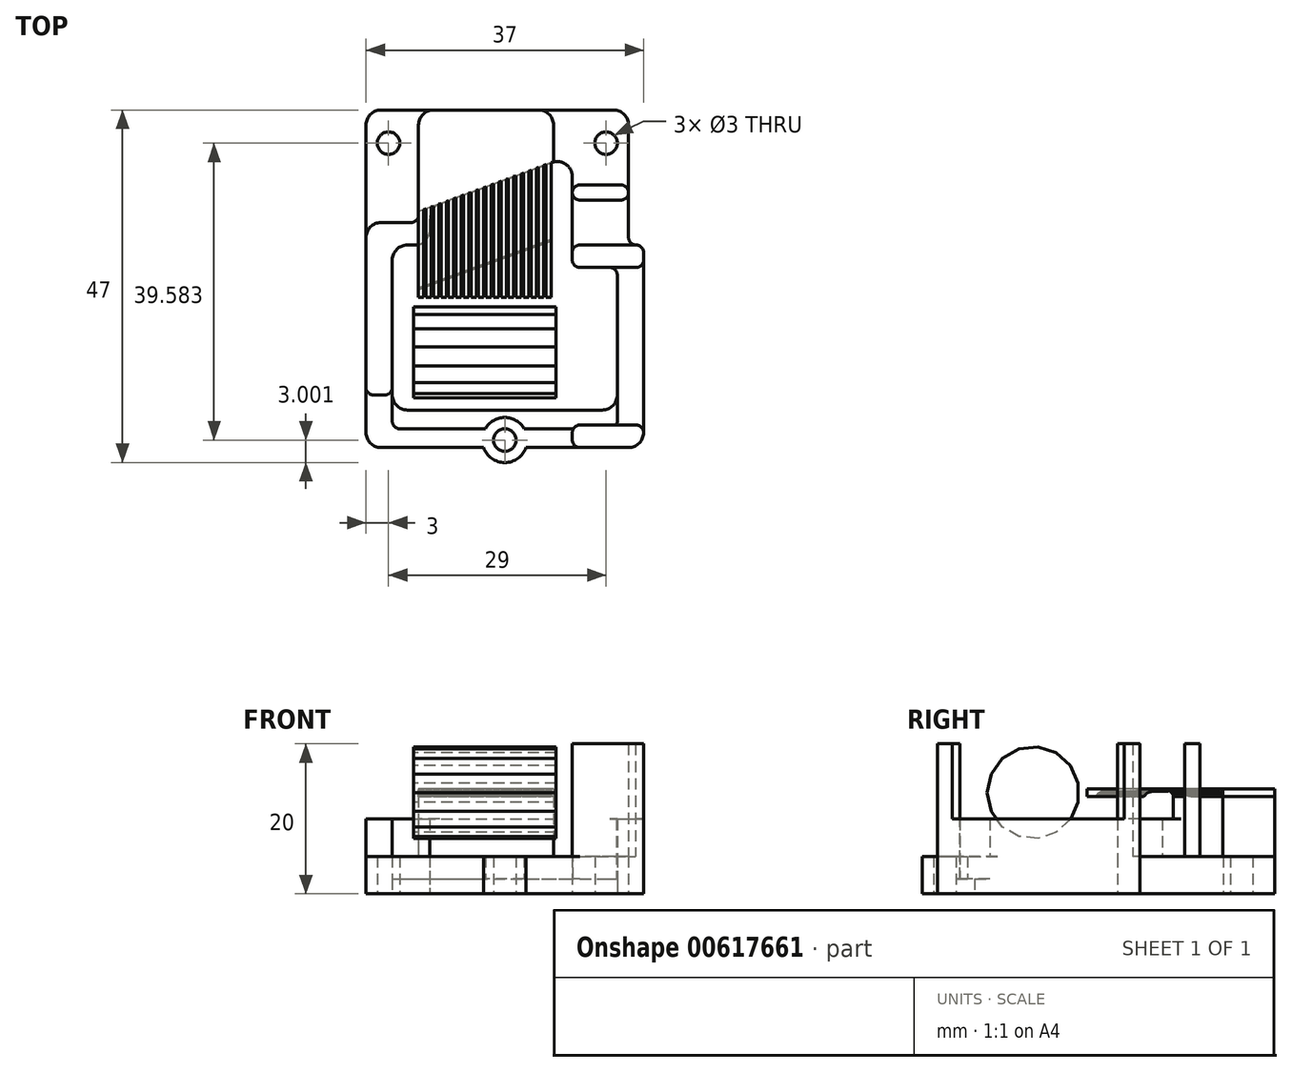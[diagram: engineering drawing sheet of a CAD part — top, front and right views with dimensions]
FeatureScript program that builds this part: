
annotation { "Feature Type Name" : "Feature", "Feature Type Description" : "" }
export const myFeature = defineFeature(function(context is Context, id is Id, definition is map)
    precondition{}
    {
        {
            var Q0;
            Q0=qCreatedBy(makeId("Top.planeOp"),FACE);
            var sketch = newSketch(context, id + "F0", { "sketchPlane" : qUnion([Q0])});
            skLineSegment(sketch, "E0.bottom", {"start": v(16.5, -22.5) * mm, "end": v(-16.5, -22.5) * mm});
            skLineSegment(sketch, "E0.top", {"start": v(14.5, 22.5) * mm, "end": v(-16.5, 22.5) * mm});
            skLineSegment(sketch, "E0.left", {"start": v(18.5, -20.5) * mm, "end": v(18.5, 3.5) * mm});
            skLineSegment(sketch, "E0.right", {"start": v(-18.5, -20.5) * mm, "end": v(-18.5, 20.5) * mm});
            skPoint(sketch, "E0.middle", {"position": v(0, 0) * mm});
            skLineSegment(sketch, "E1", {"start": v(-15, 2.5) * mm, "end": v(-15, -15.5) * mm});
            skLineSegment(sketch, "E2", {"start": v(-13, -17.5) * mm, "end": v(13, -17.5) * mm});
            skLineSegment(sketch, "E3", {"start": v(15, -15.5) * mm, "end": v(15, 0.5) * mm});
            skLineSegment(sketch, "E4", {"start": v(-13, 4.5) * mm, "end": v(-12, 4.5) * mm});
            skLineSegment(sketch, "E5", {"start": v(-10, 6.5) * mm, "end": v(-10, 8.1) * mm});
            skLineSegment(sketch, "E6", {"start": v(-8.7, 9.98) * mm, "end": v(6.3, 15.5) * mm});
            skLineSegment(sketch, "E7", {"start": v(9, 13.63) * mm, "end": v(9, 2.5) * mm});
            skLineSegment(sketch, "E8", {"start": v(10, 1.5) * mm, "end": v(14, 1.5) * mm});
            skLineSegment(sketch, "E9", {"start": v(16.5, 20.5) * mm, "end": v(16.5, 5.5) * mm});
            skLineSegment(sketch, "E10", {"start": v(17.5, 4.5) * mm, "end": v(17.5, 4.5) * mm});
            skPoint(sketch, "E11.visualSharp", {"position": v(-15, -17.5) * mm});
            skArc(sketch, "E11.filletArc", {"start": v(-15, -15.5) * mm, "mid": v(-14.41, -16.91) * mm, "end": v(-13, -17.5) * mm});
            skPoint(sketch, "E12.visualSharp", {"position": v(15, -17.5) * mm});
            skArc(sketch, "E12.filletArc", {"start": v(13, -17.5) * mm, "mid": v(14.41, -16.91) * mm, "end": v(15, -15.5) * mm});
            skPoint(sketch, "E13.visualSharp", {"position": v(-15, 4.5) * mm});
            skArc(sketch, "E13.filletArc", {"start": v(-13, 4.5) * mm, "mid": v(-14.41, 3.91) * mm, "end": v(-15, 2.5) * mm});
            skPoint(sketch, "E14.visualSharp", {"position": v(-10, 4.5) * mm});
            skArc(sketch, "E14.filletArc", {"start": v(-12, 4.5) * mm, "mid": v(-10.59, 5.09) * mm, "end": v(-10, 6.5) * mm});
            skPoint(sketch, "E15.visualSharp", {"position": v(-10, 9.5) * mm});
            skArc(sketch, "E15.filletArc", {"start": v(-8.7, 9.98) * mm, "mid": v(-9.64, 9.25) * mm, "end": v(-10, 8.1) * mm});
            skPoint(sketch, "E16.visualSharp", {"position": v(9, 16.5) * mm});
            skArc(sketch, "E16.filletArc", {"start": v(9, 13.63) * mm, "mid": v(8.14, 15.27) * mm, "end": v(6.3, 15.5) * mm});
            skPoint(sketch, "E17.visualSharp", {"position": v(-18.5, -22.5) * mm});
            skArc(sketch, "E17.filletArc", {"start": v(-18.5, -20.5) * mm, "mid": v(-17.91, -21.91) * mm, "end": v(-16.5, -22.5) * mm});
            skPoint(sketch, "E18.visualSharp", {"position": v(18.5, -22.5) * mm});
            skArc(sketch, "E18.filletArc", {"start": v(16.5, -22.5) * mm, "mid": v(17.91, -21.91) * mm, "end": v(18.5, -20.5) * mm});
            skPoint(sketch, "E19.visualSharp", {"position": v(16.5, 22.5) * mm});
            skArc(sketch, "E19.filletArc", {"start": v(16.5, 20.5) * mm, "mid": v(15.91, 21.91) * mm, "end": v(14.5, 22.5) * mm});
            skPoint(sketch, "E20.visualSharp", {"position": v(-18.5, 22.5) * mm});
            skArc(sketch, "E20.filletArc", {"start": v(-16.5, 22.5) * mm, "mid": v(-17.91, 21.91) * mm, "end": v(-18.5, 20.5) * mm});
            skPoint(sketch, "E21.visualSharp", {"position": v(9, 1.5) * mm});
            skArc(sketch, "E21.filletArc", {"start": v(9, 2.5) * mm, "mid": v(9.3, 1.8) * mm, "end": v(10, 1.5) * mm});
            skPoint(sketch, "E22.visualSharp", {"position": v(15, 1.5) * mm});
            skArc(sketch, "E22.filletArc", {"start": v(15, 0.5) * mm, "mid": v(14.7, 1.2) * mm, "end": v(14, 1.5) * mm});
            skPoint(sketch, "E23.visualSharp", {"position": v(16.5, 4.5) * mm});
            skArc(sketch, "E23.filletArc", {"start": v(16.5, 5.5) * mm, "mid": v(16.8, 4.8) * mm, "end": v(17.5, 4.5) * mm});
            skPoint(sketch, "E24.visualSharp", {"position": v(18.5, 4.5) * mm});
            skArc(sketch, "E24.filletArc", {"start": v(18.5, 3.5) * mm, "mid": v(18.2, 4.2) * mm, "end": v(17.5, 4.5) * mm});
            skLineSegment(sketch, "E25", {"start": v(-14, -20) * mm, "end": v(14, -20) * mm});
            skLineSegment(sketch, "E26", {"start": v(-15, -15.5) * mm, "end": v(-15, -19) * mm});
            skLineSegment(sketch, "E27", {"start": v(15, -15.5) * mm, "end": v(15, -19) * mm});
            skPoint(sketch, "E28.visualSharp", {"position": v(-15, -20) * mm});
            skArc(sketch, "E28.filletArc", {"start": v(-15, -19) * mm, "mid": v(-14.7, -19.7) * mm, "end": v(-14, -20) * mm});
            skPoint(sketch, "E29.visualSharp", {"position": v(15, -20) * mm});
            skArc(sketch, "E29.filletArc", {"start": v(14, -20) * mm, "mid": v(14.7, -19.7) * mm, "end": v(15, -19) * mm});
            skLineSegment(sketch, "E30", {"start": v(0, -17.5) * mm, "end": v(0, -22.96) * mm, "construction": true});
            skCircle(sketch, "E31", {"center": v(0, -21.5) * mm, "radius": 3 * mm});
            skCircle(sketch, "E32", {"center": v(0, -21.5) * mm, "radius": 1.5 * mm});
            skCircle(sketch, "E33", {"center": v(-15.5, 18.08) * mm, "radius": 3 * mm});
            skCircle(sketch, "E34", {"center": v(-15.5, 18.08) * mm, "radius": 1.5 * mm});
            skLineSegment(sketch, "E35", {"start": v(-15.5, 18.08) * mm, "end": v(14.95, 18.08) * mm, "construction": true});
            skPoint(sketch, "E36.centerSnap0", {"position": v(8.14, 15.27) * mm});
            skCircle(sketch, "E37", {"center": v(13.5, 18.08) * mm, "radius": 3 * mm});
            skCircle(sketch, "E38", {"center": v(13.5, 18.08) * mm, "radius": 1.5 * mm});
            skSolve(sketch);
        }
        {
            var Q0;
            Q0=makeQuery(id+"F0.imprint","IMPRINT",FACE,{"disambiguationData":[TD([[makeQuery(id+"F0.imprint","IMPRINT",EDGE,{"derivedFrom":sQuery(id+"F0.wireOp",EDGE,"E2")}),-1.0]])]});
            extrude(context, id + "F1", {"entities" : qUnion([Q0]), "depth" : 2 * mm, "offsetDistance" : 25 * mm});
        }
        {
            var Q0;
            Q0=makeQuery(id+"F0.imprint","IMPRINT",FACE,{"disambiguationData":[TD([[makeQuery(id+"F0.imprint","IMPRINT",EDGE,{"derivedFrom":sQuery(id+"F0.wireOp",EDGE,"E0.top")}),1.0]])]});
            var Q1;
            {var subQ0=sQuery(id+"F0.wireOp",EDGE,"E31");var subQ1=sQuery(id+"F0.wireOp",EDGE,"E0.bottom");var subQ2=makeQuery(id+"F0.imprint","INTERSECT",VERTEX,{"disambiguationData":[OD(1.0)],"derivedFrom":[subQ1,subQ0]});Q1=makeQuery(id+"F0.imprint","IMPRINT",FACE,{"disambiguationData":[TD([[makeQuery(id+"F0.imprint","IMPRINT",EDGE,{"disambiguationData":[TD([[subQ2,1.0]])],"derivedFrom":subQ1}),-1.0]])]});}
            var Q2;
            {var subQ0=sQuery(id+"F0.wireOp",EDGE,"E31");var subQ1=sQuery(id+"F0.wireOp",EDGE,"E25");var subQ2=makeQuery(id+"F0.imprint","INTERSECT",VERTEX,{"disambiguationData":[OD(0.0)],"derivedFrom":[subQ1,subQ0]});Q2=makeQuery(id+"F0.imprint","IMPRINT",FACE,{"disambiguationData":[TD([[makeQuery(id+"F0.imprint","IMPRINT",EDGE,{"disambiguationData":[TD([[subQ2,-1.0]])],"derivedFrom":subQ1}),1.0]])]});}
            var Q3;
            {var subQ0=sQuery(id+"F0.wireOp",EDGE,"E31");var subQ1=sQuery(id+"F0.wireOp",EDGE,"E0.bottom");var subQ2=makeQuery(id+"F0.imprint","INTERSECT",VERTEX,{"disambiguationData":[OD(0.0)],"derivedFrom":[subQ1,subQ0]});Q3=makeQuery(id+"F0.imprint","IMPRINT",FACE,{"disambiguationData":[TD([[makeQuery(id+"F0.imprint","IMPRINT",EDGE,{"disambiguationData":[TD([[subQ2,-1.0]])],"derivedFrom":subQ1}),-1.0]])]});}
            var Q4;
            {var subQ0=sQuery(id+"F0.wireOp",EDGE,"E31");var subQ1=sQuery(id+"F0.wireOp",EDGE,"E0.bottom");var subQ2=makeQuery(id+"F0.imprint","INTERSECT",VERTEX,{"disambiguationData":[OD(0.0)],"derivedFrom":[subQ1,subQ0]});Q4=makeQuery(id+"F0.imprint","IMPRINT",FACE,{"disambiguationData":[TD([[makeQuery(id+"F0.imprint","IMPRINT",EDGE,{"disambiguationData":[TD([[subQ2,-1.0]])],"derivedFrom":subQ1}),1.0]])]});}
            var Q5;
            Q5=makeQuery(id+"F0.imprint","IMPRINT",FACE,{"disambiguationData":[TD([[makeQuery(id+"F0.imprint","IMPRINT",EDGE,{"derivedFrom":sQuery(id+"F0.wireOp",EDGE,"E33")}),1.0]])]});
            var Q6;
            Q6=makeQuery(id+"F0.imprint","IMPRINT",FACE,{"disambiguationData":[TD([[makeQuery(id+"F0.imprint","IMPRINT",EDGE,{"derivedFrom":sQuery(id+"F0.wireOp",EDGE,"E37")}),1.0]])]});
            extrude(context, id + "F2", {"entities" : qUnion([Q0, Q1, Q2, Q3, Q4, Q5, Q6]), "operationType" : NewBodyOperationType.ADD, "depth" : 5 * mm, "offsetDistance" : 25 * mm});
        }
        {
            var Q0;
            Q0=makeQuery(id+"F2.opExtrude","CAP_FACE",FACE,{"disambiguationData":[OSD([sQuery(id+"F0.wireOp",EDGE,"E0.bottom"),sQuery(id+"F0.wireOp",EDGE,"E0.top"),sQuery(id+"F0.wireOp",EDGE,"E0.left"),sQuery(id+"F0.wireOp",EDGE,"E0.right"),sQuery(id+"F0.wireOp",EDGE,"E1"),sQuery(id+"F0.wireOp",EDGE,"E3"),sQuery(id+"F0.wireOp",EDGE,"E4"),sQuery(id+"F0.wireOp",EDGE,"E5"),sQuery(id+"F0.wireOp",EDGE,"E6"),sQuery(id+"F0.wireOp",EDGE,"E7"),sQuery(id+"F0.wireOp",EDGE,"E8"),sQuery(id+"F0.wireOp",EDGE,"E9"),sQuery(id+"F0.wireOp",EDGE,"E13.filletArc"),sQuery(id+"F0.wireOp",EDGE,"E14.filletArc"),sQuery(id+"F0.wireOp",EDGE,"E15.filletArc"),sQuery(id+"F0.wireOp",EDGE,"E16.filletArc"),sQuery(id+"F0.wireOp",EDGE,"E17.filletArc"),sQuery(id+"F0.wireOp",EDGE,"E18.filletArc"),sQuery(id+"F0.wireOp",EDGE,"E19.filletArc"),sQuery(id+"F0.wireOp",EDGE,"E20.filletArc"),sQuery(id+"F0.wireOp",EDGE,"E21.filletArc"),sQuery(id+"F0.wireOp",EDGE,"E22.filletArc"),sQuery(id+"F0.wireOp",EDGE,"E23.filletArc"),sQuery(id+"F0.wireOp",EDGE,"E24.filletArc"),sQuery(id+"F0.wireOp",EDGE,"E25"),sQuery(id+"F0.wireOp",EDGE,"E26"),sQuery(id+"F0.wireOp",EDGE,"E27"),sQuery(id+"F0.wireOp",EDGE,"E28.filletArc"),sQuery(id+"F0.wireOp",EDGE,"E29.filletArc"),sQuery(id+"F0.wireOp",EDGE,"E31"),sQuery(id+"F0.wireOp",EDGE,"E32"),sQuery(id+"F0.wireOp",EDGE,"E34"),sQuery(id+"F0.wireOp",EDGE,"E38")])],"isStart":false});
            var sketch = newSketch(context, id + "F3", { "sketchPlane" : qUnion([Q0])});
            skLineSegment(sketch, "E39", {"start": v(-17.5, -15.5) * mm, "end": v(-16, -15.5) * mm});
            skLineSegment(sketch, "E40", {"start": v(-16.5, 7.5) * mm, "end": v(-12.5, 7.5) * mm});
            skLineSegment(sketch, "E41", {"start": v(6.5, 20.5) * mm, "end": v(6.5, 15.58) * mm});
            skLineSegment(sketch, "E42", {"start": v(-11.5, 8.5) * mm, "end": v(-11.5, 20.5) * mm});
            skLineSegment(sketch, "E43", {"start": v(-9.5, 22.5) * mm, "end": v(4.5, 22.5) * mm});
            skLineSegment(sketch, "E44", {"start": v(6.5, 15.58) * mm, "end": v(-11.5, 8.95) * mm});
            skLineSegment(sketch, "E45", {"start": v(-18.5, -14.5) * mm, "end": v(-18.5, 5.5) * mm});
            skLineSegment(sketch, "E46", {"start": v(-15, -14.5) * mm, "end": v(-15, 2.5) * mm});
            skPoint(sketch, "E47.visualSharp", {"position": v(-11.5, 22.5) * mm});
            skArc(sketch, "E47.filletArc", {"start": v(-9.5, 22.5) * mm, "mid": v(-10.91, 21.91) * mm, "end": v(-11.5, 20.5) * mm});
            skPoint(sketch, "E48.visualSharp", {"position": v(6.5, 22.5) * mm});
            skArc(sketch, "E48.filletArc", {"start": v(6.5, 20.5) * mm, "mid": v(5.91, 21.91) * mm, "end": v(4.5, 22.5) * mm});
            skPoint(sketch, "E49.visualSharp", {"position": v(-15, -15.5) * mm});
            skArc(sketch, "E49.filletArc", {"start": v(-16, -15.5) * mm, "mid": v(-15.3, -15.2) * mm, "end": v(-15, -14.5) * mm});
            skPoint(sketch, "E50.visualSharp", {"position": v(-18.5, -15.5) * mm});
            skArc(sketch, "E50.filletArc", {"start": v(-18.5, -14.5) * mm, "mid": v(-18.2, -15.2) * mm, "end": v(-17.5, -15.5) * mm});
            skPoint(sketch, "E51.visualSharp", {"position": v(-18.5, 7.5) * mm});
            skArc(sketch, "E51.filletArc", {"start": v(-16.5, 7.5) * mm, "mid": v(-17.91, 6.91) * mm, "end": v(-18.5, 5.5) * mm});
            skPoint(sketch, "E52.visualSharp", {"position": v(-11.5, 7.5) * mm});
            skArc(sketch, "E52.filletArc", {"start": v(-12.5, 7.5) * mm, "mid": v(-11.8, 7.8) * mm, "end": v(-11.5, 8.5) * mm});
            skLineSegment(sketch, "E53.bottom", {"start": v(10, 12.5) * mm, "end": v(15.5, 12.5) * mm});
            skLineSegment(sketch, "E53.top", {"start": v(10, 10.5) * mm, "end": v(15.5, 10.5) * mm});
            skLineSegment(sketch, "E53.left", {"start": v(9, 11.5) * mm, "end": v(9, 11.5) * mm});
            skLineSegment(sketch, "E53.right", {"start": v(16.5, 11.5) * mm, "end": v(16.5, 11.5) * mm});
            skLineSegment(sketch, "E54.bottom", {"start": v(10, 1.5) * mm, "end": v(17.5, 1.5) * mm});
            skLineSegment(sketch, "E54.top", {"start": v(10, 4.5) * mm, "end": v(17.5, 4.5) * mm});
            skLineSegment(sketch, "E54.left", {"start": v(9, 2.5) * mm, "end": v(9, 3.5) * mm});
            skLineSegment(sketch, "E54.right", {"start": v(18.5, 2.5) * mm, "end": v(18.5, 3.5) * mm});
            skLineSegment(sketch, "E55.bottom", {"start": v(10, -19.5) * mm, "end": v(17.5, -19.5) * mm});
            skLineSegment(sketch, "E55.top", {"start": v(10, -22.5) * mm, "end": v(16.5, -22.5) * mm});
            skLineSegment(sketch, "E55.left", {"start": v(9, -20.5) * mm, "end": v(9, -21.5) * mm});
            skLineSegment(sketch, "E55.right", {"start": v(18.5, -20.5) * mm, "end": v(18.5, -20.5) * mm});
            skLineSegment(sketch, "E56.bottom", {"start": v(12.25, 4.5) * mm, "end": v(13.25, 4.5) * mm});
            skLineSegment(sketch, "E56.left", {"start": v(12.25, 4.5) * mm, "end": v(12.25, 10.5) * mm});
            skLineSegment(sketch, "E56.right", {"start": v(13.25, 4.5) * mm, "end": v(13.25, 10.5) * mm});
            skPoint(sketch, "E56.middle", {"position": v(12.75, 10.5) * mm});
            skPoint(sketch, "E57.visualSharp", {"position": v(9, 12.5) * mm});
            skArc(sketch, "E57.filletArc", {"start": v(10, 12.5) * mm, "mid": v(9.3, 12.2) * mm, "end": v(9, 11.5) * mm});
            skPoint(sketch, "E58.visualSharp", {"position": v(9, 10.5) * mm});
            skArc(sketch, "E58.filletArc", {"start": v(9, 11.5) * mm, "mid": v(9.3, 10.8) * mm, "end": v(10, 10.5) * mm});
            skPoint(sketch, "E59.visualSharp", {"position": v(16.5, 12.5) * mm});
            skArc(sketch, "E59.filletArc", {"start": v(16.5, 11.5) * mm, "mid": v(16.2, 12.2) * mm, "end": v(15.5, 12.5) * mm});
            skPoint(sketch, "E60.visualSharp", {"position": v(16.5, 10.5) * mm});
            skArc(sketch, "E60.filletArc", {"start": v(15.5, 10.5) * mm, "mid": v(16.2, 10.8) * mm, "end": v(16.5, 11.5) * mm});
            skPoint(sketch, "E61.visualSharp", {"position": v(9, 4.5) * mm});
            skArc(sketch, "E61.filletArc", {"start": v(10, 4.5) * mm, "mid": v(9.3, 4.21) * mm, "end": v(9, 3.5) * mm});
            skPoint(sketch, "E62.visualSharp", {"position": v(18.5, 1.5) * mm});
            skArc(sketch, "E62.filletArc", {"start": v(17.5, 1.5) * mm, "mid": v(18.21, 1.8) * mm, "end": v(18.5, 2.5) * mm});
            skPoint(sketch, "E63.visualSharp", {"position": v(18.5, 4.5) * mm});
            skArc(sketch, "E63.filletArc", {"start": v(18.5, 3.5) * mm, "mid": v(18.21, 4.21) * mm, "end": v(17.5, 4.5) * mm});
            skPoint(sketch, "E64.visualSharp", {"position": v(9, 1.5) * mm});
            skArc(sketch, "E64.filletArc", {"start": v(9, 2.5) * mm, "mid": v(9.3, 1.8) * mm, "end": v(10, 1.5) * mm});
            skPoint(sketch, "E65.visualSharp", {"position": v(9, -19.5) * mm});
            skArc(sketch, "E65.filletArc", {"start": v(10, -19.5) * mm, "mid": v(9.3, -19.8) * mm, "end": v(9, -20.5) * mm});
            skPoint(sketch, "E66.visualSharp", {"position": v(18.5, -19.5) * mm});
            skArc(sketch, "E66.filletArc", {"start": v(18.5, -20.5) * mm, "mid": v(18.2, -19.8) * mm, "end": v(17.5, -19.5) * mm});
            skPoint(sketch, "E67.visualSharp", {"position": v(9, -22.5) * mm});
            skArc(sketch, "E67.filletArc", {"start": v(9, -21.5) * mm, "mid": v(9.3, -22.2) * mm, "end": v(10, -22.5) * mm});
            skPoint(sketch, "E68.visualSharp", {"position": v(18.5, -22.5) * mm});
            skArc(sketch, "E68.filletArc", {"start": v(16.5, -22.5) * mm, "mid": v(17.91, -21.91) * mm, "end": v(18.5, -20.5) * mm});
            skSolve(sketch);
        }
        {
            var Q0;
            Q0=makeQuery(id+"F3.imprint","IMPRINT",FACE,{"disambiguationData":[TD([[makeQuery(id+"F3.imprint","IMPRINT",EDGE,{"derivedFrom":sQuery(id+"F3.wireOp",EDGE,"E39")}),1.0]])]});
            extrude(context, id + "F4", {"entities" : qUnion([Q0]), "operationType" : NewBodyOperationType.ADD, "depth" : 5 * mm, "offsetDistance" : 25 * mm});
        }
        {
            var Q0;
            {var subQ2=sQuery(id+"F3.wireOp",EDGE,"E41");Q0=makeQuery(id+"F3.imprint","IMPRINT",FACE,{"disambiguationData":[TD([[makeQuery(id+"F3.imprint","IMPRINT",EDGE,{"derivedFrom":subQ2}),-1.0]])]});}
            extrude(context, id + "F5", {"entities" : qUnion([Q0]), "operationType" : NewBodyOperationType.ADD, "depth" : 8 * mm, "offsetDistance" : 25 * mm});
        }
        {
            var Q0;
            {var subQ0=sQuery(id+"F3.wireOp",EDGE,"E65.filletArc");var subQ1=sQuery(id+"F3.wireOp",EDGE,"E55.bottom");var subQ2=makeQuery(id+"F3.imprint","INTERSECT",VERTEX,{"derivedFrom":[subQ1,subQ0]});Q0=makeQuery(id+"F3.imprint","IMPRINT",FACE,{"disambiguationData":[TD([[makeQuery(id+"F3.imprint","IMPRINT",EDGE,{"disambiguationData":[TD([[subQ2,-1.0]])],"derivedFrom":subQ1}),-1.0]])]});}
            var Q1;
            {var subQ9=sQuery(id+"F3.wireOp",EDGE,"E55.left");Q1=makeQuery(id+"F3.imprint","IMPRINT",FACE,{"disambiguationData":[TD([[makeQuery(id+"F3.imprint","IMPRINT",EDGE,{"derivedFrom":subQ9}),1.0]])]});}
            extrude(context, id + "F6", {"entities" : qUnion([Q0, Q1]), "operationType" : NewBodyOperationType.ADD, "oppositeDirection" : true, "depth" : 4 * mm, "offsetDistance" : 25 * mm});
        }
        {
            var Q0;
            {var subQ9=sQuery(id+"F3.wireOp",EDGE,"E55.left");Q0=makeQuery(id+"F3.imprint","IMPRINT",FACE,{"disambiguationData":[TD([[makeQuery(id+"F3.imprint","IMPRINT",EDGE,{"derivedFrom":subQ9}),1.0]])]});}
            var Q1;
            {var subQ0=sQuery(id+"F3.wireOp",EDGE,"E65.filletArc");var subQ1=sQuery(id+"F3.wireOp",EDGE,"E55.bottom");var subQ2=makeQuery(id+"F3.imprint","INTERSECT",VERTEX,{"derivedFrom":[subQ1,subQ0]});Q1=makeQuery(id+"F3.imprint","IMPRINT",FACE,{"disambiguationData":[TD([[makeQuery(id+"F3.imprint","IMPRINT",EDGE,{"disambiguationData":[TD([[subQ2,-1.0]])],"derivedFrom":subQ1}),-1.0]])]});}
            extrude(context, id + "F7", {"entities" : qUnion([Q0, Q1]), "operationType" : NewBodyOperationType.ADD, "depth" : 15 * mm, "offsetDistance" : 25 * mm});
        }
        {
            var Q0;
            {var subQ11=sQuery(id+"F3.wireOp",EDGE,"E54.bottom");Q0=makeQuery(id+"F3.imprint","IMPRINT",FACE,{"disambiguationData":[TD([[makeQuery(id+"F3.imprint","IMPRINT",EDGE,{"derivedFrom":subQ11}),1.0]])]});}
            var Q1;
            Q1=makeQuery(id+"F3.imprint","IMPRINT",FACE,{"disambiguationData":[TD([[makeQuery(id+"F3.imprint","IMPRINT",EDGE,{"derivedFrom":sQuery(id+"F3.wireOp",EDGE,"E53.bottom")}),-1.0]])]});
            extrude(context, id + "F8", {"entities" : qUnion([Q0, Q1]), "operationType" : NewBodyOperationType.ADD, "depth" : 15 * mm, "offsetDistance" : 25 * mm});
        }
        {
            var Q0;
            Q0=makeQuery(id+"F3.imprint","IMPRINT",FACE,{"disambiguationData":[TD([[makeQuery(id+"F3.imprint","IMPRINT",EDGE,{"derivedFrom":sQuery(id+"F3.wireOp",EDGE,"E56.bottom")}),1.0]])]});
            var Q1;
            {var subQ12=sQuery(id+"F3.wireOp",EDGE,"E54.bottom");Q1=makeQuery(id+"F3.imprint","IMPRINT",FACE,{"disambiguationData":[TD([[makeQuery(id+"F3.imprint","IMPRINT",EDGE,{"derivedFrom":subQ12}),-1.0]])]});}
            extrude(context, id + "F9", {"entities" : qUnion([Q0, Q1]), "operationType" : NewBodyOperationType.ADD, "depth" : 5 * mm, "offsetDistance" : 25 * mm});
        }
        {
            var Q0;
            Q0=makeQuery(id+"F5.opExtrude","CAP_FACE",FACE,{"disambiguationData":[OSD([sQuery(id+"F3.wireOp",EDGE,"E41"),sQuery(id+"F3.wireOp",EDGE,"E42"),sQuery(id+"F3.wireOp",EDGE,"E43"),sQuery(id+"F3.wireOp",EDGE,"E44"),sQuery(id+"F3.wireOp",EDGE,"E47.filletArc"),sQuery(id+"F3.wireOp",EDGE,"E48.filletArc")])],"isStart":false});
            var sketch = newSketch(context, id + "F10", { "sketchPlane" : qUnion([Q0])});
            skLineSegment(sketch, "E69.top", {"start": v(-10.8, -2.5) * mm, "end": v(-11.5, -2.5) * mm});
            skLineSegment(sketch, "E69.left", {"start": v(-10.8, 9.2) * mm, "end": v(-10.8, -2.5) * mm});
            skLineSegment(sketch, "E69.right", {"start": v(-11.5, 8.95) * mm, "end": v(-11.5, -2.5) * mm});
            skLineSegment(sketch, "E70.1.0.0", {"start": v(-9.8, 9.57) * mm, "end": v(-9.8, -2.5) * mm});
            skLineSegment(sketch, "E70.1.0.1", {"start": v(-10.5, 9.32) * mm, "end": v(-10.5, -2.5) * mm});
            skLineSegment(sketch, "E70.1.0.3", {"start": v(-9.8, -2.5) * mm, "end": v(-10.5, -2.5) * mm});
            skLineSegment(sketch, "E70.2.0.0", {"start": v(-8.8, 9.94) * mm, "end": v(-8.8, -2.5) * mm});
            skLineSegment(sketch, "E70.2.0.1", {"start": v(-9.5, 9.68) * mm, "end": v(-9.5, -2.5) * mm});
            skLineSegment(sketch, "E70.2.0.3", {"start": v(-8.8, -2.5) * mm, "end": v(-9.5, -2.5) * mm});
            skLineSegment(sketch, "E70.3.0.0", {"start": v(-7.8, 10.31) * mm, "end": v(-7.8, -2.5) * mm});
            skLineSegment(sketch, "E70.3.0.1", {"start": v(-8.5, 10.05) * mm, "end": v(-8.5, -2.5) * mm});
            skLineSegment(sketch, "E70.3.0.3", {"start": v(-7.8, -2.5) * mm, "end": v(-8.5, -2.5) * mm});
            skLineSegment(sketch, "E70.4.0.0", {"start": v(-6.8, 10.68) * mm, "end": v(-6.8, -2.5) * mm});
            skLineSegment(sketch, "E70.4.0.1", {"start": v(-7.5, 10.42) * mm, "end": v(-7.5, -2.5) * mm});
            skLineSegment(sketch, "E70.4.0.3", {"start": v(-6.8, -2.5) * mm, "end": v(-7.5, -2.5) * mm});
            skLineSegment(sketch, "E70.5.0.0", {"start": v(-5.8, 11.05) * mm, "end": v(-5.8, -2.5) * mm});
            skLineSegment(sketch, "E70.5.0.1", {"start": v(-6.5, 10.79) * mm, "end": v(-6.5, -2.5) * mm});
            skLineSegment(sketch, "E70.5.0.3", {"start": v(-5.8, -2.5) * mm, "end": v(-6.5, -2.5) * mm});
            skLineSegment(sketch, "E70.6.0.0", {"start": v(-4.8, 11.42) * mm, "end": v(-4.8, -2.5) * mm});
            skLineSegment(sketch, "E70.6.0.1", {"start": v(-5.5, 11.16) * mm, "end": v(-5.5, -2.5) * mm});
            skLineSegment(sketch, "E70.6.0.3", {"start": v(-4.8, -2.5) * mm, "end": v(-5.5, -2.5) * mm});
            skLineSegment(sketch, "E70.7.0.0", {"start": v(-3.8, 11.78) * mm, "end": v(-3.8, -2.5) * mm});
            skLineSegment(sketch, "E70.7.0.1", {"start": v(-4.5, 11.53) * mm, "end": v(-4.5, -2.5) * mm});
            skLineSegment(sketch, "E70.7.0.3", {"start": v(-3.8, -2.5) * mm, "end": v(-4.5, -2.5) * mm});
            skLineSegment(sketch, "E70.8.0.0", {"start": v(-2.8, 12.15) * mm, "end": v(-2.8, -2.5) * mm});
            skLineSegment(sketch, "E70.8.0.1", {"start": v(-3.5, 11.9) * mm, "end": v(-3.5, -2.5) * mm});
            skLineSegment(sketch, "E70.8.0.3", {"start": v(-2.8, -2.5) * mm, "end": v(-3.5, -2.5) * mm});
            skLineSegment(sketch, "E70.9.0.0", {"start": v(-1.8, 12.52) * mm, "end": v(-1.8, -2.5) * mm});
            skLineSegment(sketch, "E70.9.0.1", {"start": v(-2.5, 12.26) * mm, "end": v(-2.5, -2.5) * mm});
            skLineSegment(sketch, "E70.9.0.3", {"start": v(-1.8, -2.5) * mm, "end": v(-2.5, -2.5) * mm});
            skLineSegment(sketch, "E70.10.0.0", {"start": v(-0.8, 12.89) * mm, "end": v(-0.8, -2.5) * mm});
            skLineSegment(sketch, "E70.10.0.1", {"start": v(-1.5, 12.63) * mm, "end": v(-1.5, -2.5) * mm});
            skLineSegment(sketch, "E70.10.0.3", {"start": v(-0.8, -2.5) * mm, "end": v(-1.5, -2.5) * mm});
            skLineSegment(sketch, "E70.11.0.0", {"start": v(0.2, 13.26) * mm, "end": v(0.2, -2.5) * mm});
            skLineSegment(sketch, "E70.11.0.1", {"start": v(-0.5, 13) * mm, "end": v(-0.5, -2.5) * mm});
            skLineSegment(sketch, "E70.11.0.3", {"start": v(0.2, -2.5) * mm, "end": v(-0.5, -2.5) * mm});
            skLineSegment(sketch, "E70.12.0.0", {"start": v(1.2, 13.63) * mm, "end": v(1.2, -2.5) * mm});
            skLineSegment(sketch, "E70.12.0.1", {"start": v(0.5, 13.37) * mm, "end": v(0.5, -2.5) * mm});
            skLineSegment(sketch, "E70.12.0.3", {"start": v(1.2, -2.5) * mm, "end": v(0.5, -2.5) * mm});
            skLineSegment(sketch, "E70.13.0.0", {"start": v(2.2, 14) * mm, "end": v(2.2, -2.5) * mm});
            skLineSegment(sketch, "E70.13.0.1", {"start": v(1.5, 13.74) * mm, "end": v(1.5, -2.5) * mm});
            skLineSegment(sketch, "E70.13.0.3", {"start": v(2.2, -2.5) * mm, "end": v(1.5, -2.5) * mm});
            skLineSegment(sketch, "E70.14.0.0", {"start": v(3.2, 14.36) * mm, "end": v(3.2, -2.5) * mm});
            skLineSegment(sketch, "E70.14.0.1", {"start": v(2.5, 14.1) * mm, "end": v(2.5, -2.5) * mm});
            skLineSegment(sketch, "E70.14.0.3", {"start": v(3.2, -2.5) * mm, "end": v(2.5, -2.5) * mm});
            skLineSegment(sketch, "E70.15.0.0", {"start": v(4.2, 14.73) * mm, "end": v(4.2, -2.5) * mm});
            skLineSegment(sketch, "E70.15.0.1", {"start": v(3.5, 14.47) * mm, "end": v(3.5, -2.5) * mm});
            skLineSegment(sketch, "E70.15.0.3", {"start": v(4.2, -2.5) * mm, "end": v(3.5, -2.5) * mm});
            skLineSegment(sketch, "E70.16.0.0", {"start": v(5.2, 15.1) * mm, "end": v(5.2, -2.5) * mm});
            skLineSegment(sketch, "E70.16.0.1", {"start": v(4.5, 14.84) * mm, "end": v(4.5, -2.5) * mm});
            skLineSegment(sketch, "E70.16.0.3", {"start": v(5.2, -2.5) * mm, "end": v(4.5, -2.5) * mm});
            skLineSegment(sketch, "E70.17.0.0", {"start": v(6.2, 15.47) * mm, "end": v(6.2, -2.5) * mm});
            skLineSegment(sketch, "E70.17.0.1", {"start": v(5.5, 15.21) * mm, "end": v(5.5, -2.5) * mm});
            skLineSegment(sketch, "E70.17.0.3", {"start": v(6.2, -2.5) * mm, "end": v(5.5, -2.5) * mm});
            skLineSegment(sketch, "E70.direction1", {"start": v(-11.5, -2.5) * mm, "end": v(-10.5, -2.5) * mm, "construction": true});
            skLineSegment(sketch, "E71", {"start": v(-11.5, 8.95) * mm, "end": v(6.5, 15.58) * mm});
            skSolve(sketch);
        }
        {
            var Q0;
            {var subQ0=sQuery(id+"F10.wireOp",EDGE,"E70.15.0.0");Q0=makeQuery(id+"F10.imprint","IMPRINT",FACE,{"disambiguationData":[TD([[makeQuery(id+"F10.imprint","IMPRINT",EDGE,{"derivedFrom":subQ0}),-1.0]])]});}
            var Q1;
            {var subQ0=sQuery(id+"F10.wireOp",EDGE,"E70.13.0.0");Q1=makeQuery(id+"F10.imprint","IMPRINT",FACE,{"disambiguationData":[TD([[makeQuery(id+"F10.imprint","IMPRINT",EDGE,{"derivedFrom":subQ0}),-1.0]])]});}
            var Q2;
            {var subQ0=sQuery(id+"F10.wireOp",EDGE,"E70.14.0.0");Q2=makeQuery(id+"F10.imprint","IMPRINT",FACE,{"disambiguationData":[TD([[makeQuery(id+"F10.imprint","IMPRINT",EDGE,{"derivedFrom":subQ0}),-1.0]])]});}
            var Q3;
            Q3=makeQuery(id+"F10.imprint","IMPRINT",FACE,{"disambiguationData":[TD([[makeQuery(id+"F10.imprint","IMPRINT",EDGE,{"derivedFrom":sQuery(id+"F10.wireOp",EDGE,"E69.top")}),-1.0]])]});
            var Q4;
            {var subQ0=sQuery(id+"F10.wireOp",EDGE,"E70.1.0.0");Q4=makeQuery(id+"F10.imprint","IMPRINT",FACE,{"disambiguationData":[TD([[makeQuery(id+"F10.imprint","IMPRINT",EDGE,{"derivedFrom":subQ0}),-1.0]])]});}
            var Q5;
            {var subQ0=sQuery(id+"F10.wireOp",EDGE,"E70.2.0.0");Q5=makeQuery(id+"F10.imprint","IMPRINT",FACE,{"disambiguationData":[TD([[makeQuery(id+"F10.imprint","IMPRINT",EDGE,{"derivedFrom":subQ0}),-1.0]])]});}
            var Q6;
            {var subQ0=sQuery(id+"F10.wireOp",EDGE,"E70.3.0.0");Q6=makeQuery(id+"F10.imprint","IMPRINT",FACE,{"disambiguationData":[TD([[makeQuery(id+"F10.imprint","IMPRINT",EDGE,{"derivedFrom":subQ0}),-1.0]])]});}
            var Q7;
            {var subQ0=sQuery(id+"F10.wireOp",EDGE,"E70.4.0.0");Q7=makeQuery(id+"F10.imprint","IMPRINT",FACE,{"disambiguationData":[TD([[makeQuery(id+"F10.imprint","IMPRINT",EDGE,{"derivedFrom":subQ0}),-1.0]])]});}
            var Q8;
            {var subQ0=sQuery(id+"F10.wireOp",EDGE,"E70.5.0.0");Q8=makeQuery(id+"F10.imprint","IMPRINT",FACE,{"disambiguationData":[TD([[makeQuery(id+"F10.imprint","IMPRINT",EDGE,{"derivedFrom":subQ0}),-1.0]])]});}
            var Q9;
            {var subQ0=sQuery(id+"F10.wireOp",EDGE,"E70.6.0.0");Q9=makeQuery(id+"F10.imprint","IMPRINT",FACE,{"disambiguationData":[TD([[makeQuery(id+"F10.imprint","IMPRINT",EDGE,{"derivedFrom":subQ0}),-1.0]])]});}
            var Q10;
            {var subQ0=sQuery(id+"F10.wireOp",EDGE,"E70.7.0.0");Q10=makeQuery(id+"F10.imprint","IMPRINT",FACE,{"disambiguationData":[TD([[makeQuery(id+"F10.imprint","IMPRINT",EDGE,{"derivedFrom":subQ0}),-1.0]])]});}
            var Q11;
            {var subQ0=sQuery(id+"F10.wireOp",EDGE,"E70.8.0.0");Q11=makeQuery(id+"F10.imprint","IMPRINT",FACE,{"disambiguationData":[TD([[makeQuery(id+"F10.imprint","IMPRINT",EDGE,{"derivedFrom":subQ0}),-1.0]])]});}
            var Q12;
            {var subQ0=sQuery(id+"F10.wireOp",EDGE,"E70.9.0.0");Q12=makeQuery(id+"F10.imprint","IMPRINT",FACE,{"disambiguationData":[TD([[makeQuery(id+"F10.imprint","IMPRINT",EDGE,{"derivedFrom":subQ0}),-1.0]])]});}
            var Q13;
            {var subQ0=sQuery(id+"F10.wireOp",EDGE,"E70.10.0.0");Q13=makeQuery(id+"F10.imprint","IMPRINT",FACE,{"disambiguationData":[TD([[makeQuery(id+"F10.imprint","IMPRINT",EDGE,{"derivedFrom":subQ0}),-1.0]])]});}
            var Q14;
            {var subQ0=sQuery(id+"F10.wireOp",EDGE,"E70.11.0.0");Q14=makeQuery(id+"F10.imprint","IMPRINT",FACE,{"disambiguationData":[TD([[makeQuery(id+"F10.imprint","IMPRINT",EDGE,{"derivedFrom":subQ0}),-1.0]])]});}
            var Q15;
            {var subQ0=sQuery(id+"F10.wireOp",EDGE,"E70.12.0.0");Q15=makeQuery(id+"F10.imprint","IMPRINT",FACE,{"disambiguationData":[TD([[makeQuery(id+"F10.imprint","IMPRINT",EDGE,{"derivedFrom":subQ0}),-1.0]])]});}
            var Q16;
            {var subQ0=sQuery(id+"F10.wireOp",EDGE,"E70.16.0.0");Q16=makeQuery(id+"F10.imprint","IMPRINT",FACE,{"disambiguationData":[TD([[makeQuery(id+"F10.imprint","IMPRINT",EDGE,{"derivedFrom":subQ0}),-1.0]])]});}
            var Q17;
            {var subQ0=sQuery(id+"F10.wireOp",EDGE,"E70.17.0.0");Q17=makeQuery(id+"F10.imprint","IMPRINT",FACE,{"disambiguationData":[TD([[makeQuery(id+"F10.imprint","IMPRINT",EDGE,{"derivedFrom":subQ0}),-1.0]])]});}
            var Q18;
            {var subQ18=makeQuery(id+"F5.opExtrude","CAP_EDGE",EDGE,{"disambiguationData":[OSD([sQuery(id+"F3.wireOp",EDGE,"E41")])],"isStart":false});Q18=makeQuery(id+"F10.imprint","IMPRINT",FACE,{"disambiguationData":[TD([[makeQuery(id+"F10.imprint","IMPRINT",EDGE,{"derivedFrom":subQ18}),-1.0]])]});}
            extrude(context, id + "F11", {"entities" : qUnion([Q0, Q1, Q2, Q3, Q4, Q5, Q6, Q7, Q8, Q9, Q10, Q11, Q12, Q13, Q14, Q15, Q16, Q17, Q18]), "depth" : 1 * mm, "offsetDistance" : 25 * mm});
        }
        {
            var Q0;
            Q0=makeQuery(id+"F11.opExtrude","SWEPT_FACE",FACE,{"disambiguationData":[OSD([sQuery(id+"F3.wireOp",EDGE,"E42"),sQuery(id+"F10.wireOp",EDGE,"E69.right")])]});
            var sketch = newSketch(context, id + "F12", { "sketchPlane" : qUnion([Q0])});
            skLineSegment(sketch, "E72", {"start": v(-9, 13) * mm, "end": v(-8.97, 13.1) * mm});
            skLineSegment(sketch, "E73", {"start": v(-7.92, 13.83) * mm, "end": v(0.43, 13.62) * mm});
            skLineSegment(sketch, "E74", {"start": v(1.2, 13.26) * mm, "end": v(1.44, 13) * mm});
            skPoint(sketch, "E75.visualSharp", {"position": v(-8.71, 13.85) * mm});
            skArc(sketch, "E75.filletArc", {"start": v(-7.92, 13.83) * mm, "mid": v(-8.56, 13.64) * mm, "end": v(-8.97, 13.1) * mm});
            skPoint(sketch, "E76.visualSharp", {"position": v(0.9, 13.6) * mm});
            skArc(sketch, "E76.filletArc", {"start": v(1.2, 13.26) * mm, "mid": v(0.86, 13.52) * mm, "end": v(0.43, 13.62) * mm});
            skSolve(sketch);
        }
        {
            var Q0;
            Q0=makeQuery(id+"F11.opExtrude","CAP_FACE",FACE,{"disambiguationData":[OSD([sQuery(id+"F3.wireOp",EDGE,"E41"),sQuery(id+"F3.wireOp",EDGE,"E42"),sQuery(id+"F3.wireOp",EDGE,"E43"),sQuery(id+"F3.wireOp",EDGE,"E47.filletArc"),sQuery(id+"F3.wireOp",EDGE,"E48.filletArc"),sQuery(id+"F10.wireOp",EDGE,"E69.top"),sQuery(id+"F10.wireOp",EDGE,"E69.left"),sQuery(id+"F10.wireOp",EDGE,"E69.right"),sQuery(id+"F10.wireOp",EDGE,"E70.1.0.0"),sQuery(id+"F10.wireOp",EDGE,"E70.1.0.1"),sQuery(id+"F10.wireOp",EDGE,"E70.1.0.3"),sQuery(id+"F10.wireOp",EDGE,"E70.2.0.0"),sQuery(id+"F10.wireOp",EDGE,"E70.2.0.1"),sQuery(id+"F10.wireOp",EDGE,"E70.2.0.3"),sQuery(id+"F10.wireOp",EDGE,"E70.3.0.0"),sQuery(id+"F10.wireOp",EDGE,"E70.3.0.1"),sQuery(id+"F10.wireOp",EDGE,"E70.3.0.3"),sQuery(id+"F10.wireOp",EDGE,"E70.4.0.0"),sQuery(id+"F10.wireOp",EDGE,"E70.4.0.1"),sQuery(id+"F10.wireOp",EDGE,"E70.4.0.3"),sQuery(id+"F10.wireOp",EDGE,"E70.5.0.0"),sQuery(id+"F10.wireOp",EDGE,"E70.5.0.1"),sQuery(id+"F10.wireOp",EDGE,"E70.5.0.3"),sQuery(id+"F10.wireOp",EDGE,"E70.6.0.0"),sQuery(id+"F10.wireOp",EDGE,"E70.6.0.1"),sQuery(id+"F10.wireOp",EDGE,"E70.6.0.3"),sQuery(id+"F10.wireOp",EDGE,"E70.7.0.0"),sQuery(id+"F10.wireOp",EDGE,"E70.7.0.1"),sQuery(id+"F10.wireOp",EDGE,"E70.7.0.3"),sQuery(id+"F10.wireOp",EDGE,"E70.8.0.0"),sQuery(id+"F10.wireOp",EDGE,"E70.8.0.1"),sQuery(id+"F10.wireOp",EDGE,"E70.8.0.3"),sQuery(id+"F10.wireOp",EDGE,"E70.9.0.0"),sQuery(id+"F10.wireOp",EDGE,"E70.9.0.1"),sQuery(id+"F10.wireOp",EDGE,"E70.9.0.3"),sQuery(id+"F10.wireOp",EDGE,"E70.10.0.0"),sQuery(id+"F10.wireOp",EDGE,"E70.10.0.1"),sQuery(id+"F10.wireOp",EDGE,"E70.10.0.3"),sQuery(id+"F10.wireOp",EDGE,"E70.11.0.0"),sQuery(id+"F10.wireOp",EDGE,"E70.11.0.1"),sQuery(id+"F10.wireOp",EDGE,"E70.11.0.3"),sQuery(id+"F10.wireOp",EDGE,"E70.12.0.0"),sQuery(id+"F10.wireOp",EDGE,"E70.12.0.1"),sQuery(id+"F10.wireOp",EDGE,"E70.12.0.3"),sQuery(id+"F10.wireOp",EDGE,"E70.13.0.0"),sQuery(id+"F10.wireOp",EDGE,"E70.13.0.1"),sQuery(id+"F10.wireOp",EDGE,"E70.13.0.3"),sQuery(id+"F10.wireOp",EDGE,"E70.14.0.0"),sQuery(id+"F10.wireOp",EDGE,"E70.14.0.1"),sQuery(id+"F10.wireOp",EDGE,"E70.14.0.3"),sQuery(id+"F10.wireOp",EDGE,"E70.15.0.0"),sQuery(id+"F10.wireOp",EDGE,"E70.15.0.1"),sQuery(id+"F10.wireOp",EDGE,"E70.15.0.3"),sQuery(id+"F10.wireOp",EDGE,"E70.16.0.0"),sQuery(id+"F10.wireOp",EDGE,"E70.16.0.1"),sQuery(id+"F10.wireOp",EDGE,"E70.16.0.3"),sQuery(id+"F10.wireOp",EDGE,"E70.17.0.0"),sQuery(id+"F10.wireOp",EDGE,"E70.17.0.1"),sQuery(id+"F10.wireOp",EDGE,"E70.17.0.3"),sQuery(id+"F10.wireOp",EDGE,"E71")])],"isStart":true});
            var sketch = newSketch(context, id + "F13", { "sketchPlane" : qUnion([Q0])});
            skLineSegment(sketch, "E77", {"start": v(-11.5, -9) * mm, "end": v(6.5, -15.58) * mm});
            skSolve(sketch);
        }
        {
            var Q0;
            {var subQ1=sQuery(id+"F12.wireOp",EDGE,"E72");Q0=makeQuery(id+"F12.imprint","IMPRINT",FACE,{"disambiguationData":[TD([[makeQuery(id+"F12.imprint","IMPRINT",EDGE,{"derivedFrom":subQ1}),-1.0]])]});}
            var Q1;
            Q1=sQuery(id+"F13.wireOp",EDGE,"E77");
            sweep(context, id + "F14", {"operationType" : NewBodyOperationType.REMOVE, "profiles" : qUnion([Q0]), "path" : qUnion([Q1])});
        }
        {
            var Q0;
            Q0=makeQuery(id+"F11.opExtrude","SWEPT_FACE",FACE,{"disambiguationData":[OSD([sQuery(id+"F10.wireOp",EDGE,"E70.17.0.0")])]});
            var Q1;
            Q1=makeQuery(id+"F11.opExtrude","SWEPT_FACE",FACE,{"disambiguationData":[OSD([sQuery(id+"F3.wireOp",EDGE,"E42"),sQuery(id+"F10.wireOp",EDGE,"E69.right")])]});
            cPlane(context, id + "F15", {"entities" : qUnion([Q0, Q1]), "cplaneType" : CPlaneType.MID_PLANE, "offset" : 25 * mm, "width" : 150 * mm, "height" : 150 * mm});
        }
        {
            var Q0;
            Q0=qCreatedBy(id+"F15.planeOp",FACE);
            var sketch = newSketch(context, id + "F16", { "sketchPlane" : qUnion([Q0])});
            skLineSegment(sketch, "E78", {"start": v(-2.5, 13.5) * mm, "end": v(-16.95, 13.5) * mm, "construction": true});
            skCircle(sketch, "E79.cCircle", {"center": v(-9.72, 13.5) * mm, "radius": 6 * mm, "construction": true});
            skLineSegment(sketch, "E79.0", {"start": v(-4.76, 9.9) * mm, "end": v(-6.65, 8.2) * mm});
            skLineSegment(sketch, "E79.1", {"start": v(-6.65, 8.2) * mm, "end": v(-9.08, 7.4) * mm});
            skLineSegment(sketch, "E79.2", {"start": v(-9.08, 7.4) * mm, "end": v(-11.61, 7.66) * mm});
            skLineSegment(sketch, "E79.3", {"start": v(-11.61, 7.66) * mm, "end": v(-13.82, 8.94) * mm});
            skLineSegment(sketch, "E79.4", {"start": v(-13.82, 8.94) * mm, "end": v(-15.32, 11) * mm});
            skLineSegment(sketch, "E79.5", {"start": v(-15.32, 11) * mm, "end": v(-15.86, 13.5) * mm});
            skLineSegment(sketch, "E79.6", {"start": v(-15.86, 13.5) * mm, "end": v(-15.33, 16) * mm});
            skLineSegment(sketch, "E79.7", {"start": v(-15.33, 16) * mm, "end": v(-13.83, 18.06) * mm});
            skLineSegment(sketch, "E79.8", {"start": v(-13.83, 18.06) * mm, "end": v(-11.62, 19.33) * mm});
            skLineSegment(sketch, "E79.9", {"start": v(-11.62, 19.33) * mm, "end": v(-9.09, 19.6) * mm});
            skLineSegment(sketch, "E79.10", {"start": v(-9.09, 19.6) * mm, "end": v(-6.66, 18.81) * mm});
            skLineSegment(sketch, "E79.11", {"start": v(-6.66, 18.81) * mm, "end": v(-4.76, 17.1) * mm});
            skLineSegment(sketch, "E79.12", {"start": v(-4.76, 17.1) * mm, "end": v(-3.72, 14.78) * mm});
            skLineSegment(sketch, "E79.13", {"start": v(-3.72, 14.78) * mm, "end": v(-3.72, 12.23) * mm});
            skLineSegment(sketch, "E79.14", {"start": v(-3.72, 12.23) * mm, "end": v(-4.76, 9.9) * mm});
            skPoint(sketch, "E79.0.midPoint", {"position": v(-5.7, 9.04) * mm});
            skSolve(sketch);
        }
        {
            var Q0;
            Q0=makeQuery(id+"F16.imprint","IMPRINT",FACE,{"disambiguationData":[TD([[makeQuery(id+"F16.imprint","IMPRINT",EDGE,{"derivedFrom":sQuery(id+"F16.wireOp",EDGE,"E79.0")}),-1.0]])]});
            extrude(context, id + "F17", {"entities" : qUnion([Q0]), "endBound" : BoundingType.SYMMETRIC, "depth" : 19 * mm, "offsetDistance" : 25 * mm});
        }
    });
